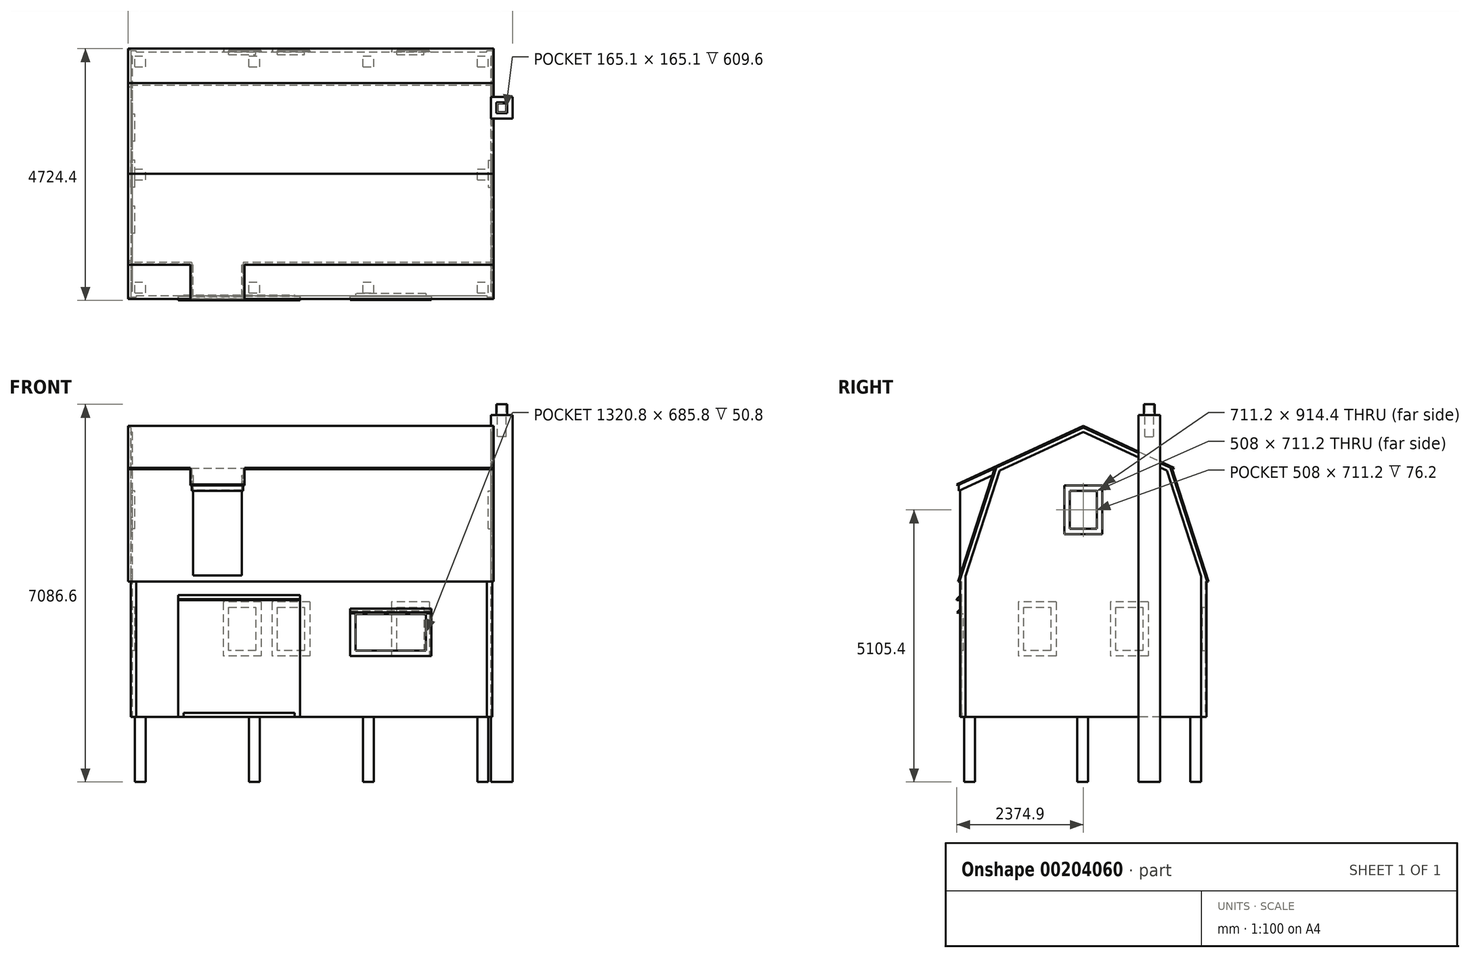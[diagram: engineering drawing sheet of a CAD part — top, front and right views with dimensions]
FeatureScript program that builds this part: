
annotation { "Feature Type Name" : "Feature", "Feature Type Description" : "" }
export const myFeature = defineFeature(function(context is Context, id is Id, definition is map)
    precondition{}
    {
        {
            var Q0;
            Q0=qCreatedBy(makeId("Right.planeOp"),FACE);
            var sketch = newSketch(context, id + "F0", { "sketchPlane" : qUnion([Q0])});
            skLineSegment(sketch, "E0", {"start": v(0, 0) * mm, "end": v(0, 2540) * mm});
            skLineSegment(sketch, "E1", {"start": v(0, 2540) * mm, "end": v(698.5, 4699) * mm});
            skLineSegment(sketch, "E2", {"start": v(698.5, 4699) * mm, "end": v(2349.5, 5461) * mm});
            skLineSegment(sketch, "E3", {"start": v(2349.5, 5461) * mm, "end": v(4000.5, 4699) * mm});
            skLineSegment(sketch, "E4", {"start": v(4000.5, 4699) * mm, "end": v(4699, 2540) * mm});
            skLineSegment(sketch, "E5", {"start": v(4699, 2540) * mm, "end": v(4699, 0) * mm});
            skLineSegment(sketch, "E6", {"start": v(4699, 0) * mm, "end": v(0, 0) * mm});
            skLineSegment(sketch, "E7", {"start": v(2349.5, 5461) * mm, "end": v(2349.5, 0) * mm, "construction": true});
            skSolve(sketch);
        }
        {
            var Q0;
            Q0 = qSketchRegion(id + "F0", true);
            extrude(context, id + "F1", {"entities" : qUnion([Q0]), "depth" : 6781.8 * mm});
        }
        {
            var Q0;
            Q0=makeQuery(id+"F1.opExtrude","CAP_FACE",FACE,{"disambiguationData":[OSD([sQuery(id+"F0.wireOp",EDGE,"E0"),sQuery(id+"F0.wireOp",EDGE,"E1"),sQuery(id+"F0.wireOp",EDGE,"E2"),sQuery(id+"F0.wireOp",EDGE,"E3"),sQuery(id+"F0.wireOp",EDGE,"E4"),sQuery(id+"F0.wireOp",EDGE,"E5"),sQuery(id+"F0.wireOp",EDGE,"E6")])],"isStart":false});
            var sketch = newSketch(context, id + "F2", { "sketchPlane" : qUnion([Q0])});
            skLineSegment(sketch, "E8.bottom", {"start": v(0, 2540) * mm, "end": v(38.1, 2540) * mm});
            skLineSegment(sketch, "E8.top", {"start": v(0, 0) * mm, "end": v(38.1, 0) * mm});
            skLineSegment(sketch, "E8.left", {"start": v(0, 2540) * mm, "end": v(0, 0) * mm});
            skLineSegment(sketch, "E8.right", {"start": v(38.1, 2540) * mm, "end": v(38.1, 0) * mm});
            skLineSegment(sketch, "E9", {"start": v(2349.5, 5461) * mm, "end": v(2349.5, 4550.7) * mm, "construction": true});
            skLineSegment(sketch, "E10.MirrorCS", {"start": v(4660.9, 2540) * mm, "end": v(4660.9, 0) * mm});
            skLineSegment(sketch, "E11.MirrorCS", {"start": v(4699, 2540) * mm, "end": v(4699, 0) * mm});
            skLineSegment(sketch, "E12.MirrorCS", {"start": v(4699, 0) * mm, "end": v(4660.9, 0) * mm});
            skLineSegment(sketch, "E13.MirrorCS", {"start": v(4699, 2540) * mm, "end": v(4660.9, 2540) * mm});
            skSolve(sketch);
        }
        {
            var Q0;
            Q0 = qSketchRegion(id + "F2", true);
            extrude(context, id + "F3", {"entities" : qUnion([Q0]), "operationType" : NewBodyOperationType.REMOVE, "endBound" : BoundingType.THROUGH_ALL, "oppositeDirection" : true, "depth" : 25.4 * mm});
        }
        {
            var Q0;
            Q0=makeQuery(id+"F1.opExtrude","CAP_FACE",FACE,{"disambiguationData":[OSD([sQuery(id+"F0.wireOp",EDGE,"E0"),sQuery(id+"F0.wireOp",EDGE,"E1"),sQuery(id+"F0.wireOp",EDGE,"E2"),sQuery(id+"F0.wireOp",EDGE,"E3"),sQuery(id+"F0.wireOp",EDGE,"E4"),sQuery(id+"F0.wireOp",EDGE,"E5"),sQuery(id+"F0.wireOp",EDGE,"E6")])],"isStart":false});
            var sketch = newSketch(context, id + "F4", { "sketchPlane" : qUnion([Q0])});
            skLineSegment(sketch, "E14", {"start": v(139.7, 0) * mm, "end": v(139.7, 2641.74) * mm});
            skLineSegment(sketch, "E15", {"start": v(139.7, 2641.74) * mm, "end": v(781.47, 4625.4) * mm});
            skLineSegment(sketch, "E16", {"start": v(781.47, 4625.4) * mm, "end": v(2349.5, 5349.1) * mm});
            skLineSegment(sketch, "E17", {"start": v(2349.5, 5349.1) * mm, "end": v(3917.53, 4625.4) * mm});
            skLineSegment(sketch, "E18", {"start": v(3917.53, 4625.4) * mm, "end": v(4559.3, 2641.74) * mm});
            skLineSegment(sketch, "E19", {"start": v(4559.3, 2641.74) * mm, "end": v(4559.3, 0) * mm});
            skSolve(sketch);
        }
        {
            var Q0;
            {var subQ0=sQuery(id+"F4.wireOp",EDGE,"E14");Q0=makeQuery(id+"F4.imprint","IMPRINT",FACE,{"disambiguationData":[TD([[makeQuery(id+"F4.imprint","IMPRINT",EDGE,{"derivedFrom":subQ0}),-1.0]])]});}
            var Q1;
            Q1 = qSketchRegion(id + "F4", true);
            extrude(context, id + "F5", {"entities" : qUnion([Q0, Q1]), "operationType" : NewBodyOperationType.REMOVE, "oppositeDirection" : true, "depth" : 25.4 * mm});
        }
        {
            var Q0;
            Q0=makeQuery(id+"F1.opExtrude","CAP_FACE",FACE,{"disambiguationData":[OSD([sQuery(id+"F0.wireOp",EDGE,"E0"),sQuery(id+"F0.wireOp",EDGE,"E1"),sQuery(id+"F0.wireOp",EDGE,"E2"),sQuery(id+"F0.wireOp",EDGE,"E3"),sQuery(id+"F0.wireOp",EDGE,"E4"),sQuery(id+"F0.wireOp",EDGE,"E5"),sQuery(id+"F0.wireOp",EDGE,"E6")])],"isStart":true});
            var sketch = newSketch(context, id + "F6", { "sketchPlane" : qUnion([Q0])});
            skLineSegment(sketch, "E20.0.0", {"start": v(-139.7, 2641.74) * mm, "end": v(-139.7, 0) * mm});
            skLineSegment(sketch, "E20.0.1", {"start": v(-139.7, 0) * mm, "end": v(-4559.3, 0) * mm});
            skLineSegment(sketch, "E20.0.2", {"start": v(-4559.3, 0) * mm, "end": v(-4559.3, 2641.74) * mm});
            skLineSegment(sketch, "E20.0.3", {"start": v(-4559.3, 2641.74) * mm, "end": v(-3917.53, 4625.4) * mm});
            skLineSegment(sketch, "E20.0.4", {"start": v(-3917.53, 4625.4) * mm, "end": v(-2349.5, 5349.1) * mm});
            skLineSegment(sketch, "E20.0.5", {"start": v(-2349.5, 5349.1) * mm, "end": v(-781.47, 4625.4) * mm});
            skLineSegment(sketch, "E20.0.6", {"start": v(-781.47, 4625.4) * mm, "end": v(-139.7, 2641.74) * mm});
            skSolve(sketch);
        }
        {
            var Q0;
            Q0 = qSketchRegion(id + "F6", true);
            extrude(context, id + "F7", {"entities" : qUnion([Q0]), "operationType" : NewBodyOperationType.REMOVE, "oppositeDirection" : true, "depth" : 25.4 * mm});
        }
        {
            var Q0;
            Q0=makeQuery(id+"F1.opExtrude","CAP_FACE",FACE,{"disambiguationData":[OSD([sQuery(id+"F0.wireOp",EDGE,"E0"),sQuery(id+"F0.wireOp",EDGE,"E1"),sQuery(id+"F0.wireOp",EDGE,"E2"),sQuery(id+"F0.wireOp",EDGE,"E3"),sQuery(id+"F0.wireOp",EDGE,"E4"),sQuery(id+"F0.wireOp",EDGE,"E5"),sQuery(id+"F0.wireOp",EDGE,"E6")])],"isStart":false});
            var sketch = newSketch(context, id + "F8", { "sketchPlane" : qUnion([Q0])});
            skLineSegment(sketch, "E21", {"start": v(26.7, 2540) * mm, "end": v(719.24, 4680.6) * mm});
            skLineSegment(sketch, "E22", {"start": v(719.24, 4680.6) * mm, "end": v(2349.5, 5433.03) * mm});
            skLineSegment(sketch, "E23", {"start": v(2349.5, 5433.03) * mm, "end": v(3979.76, 4680.6) * mm});
            skLineSegment(sketch, "E24", {"start": v(3979.76, 4680.6) * mm, "end": v(4672.3, 2540) * mm});
            skLineSegment(sketch, "E25", {"start": v(4672.3, 2540) * mm, "end": v(4699, 2540) * mm});
            skLineSegment(sketch, "E26", {"start": v(26.7, 2540) * mm, "end": v(0, 2540) * mm});
            skLineSegment(sketch, "E27", {"start": v(698.5, 4699) * mm, "end": v(645.83, 4674.7) * mm});
            skLineSegment(sketch, "E28", {"start": v(645.83, 4674.7) * mm, "end": v(656.48, 4651.63) * mm});
            skLineSegment(sketch, "E29", {"start": v(656.48, 4651.63) * mm, "end": v(687.86, 4666.11) * mm});
            skLineSegment(sketch, "E30", {"start": v(2349.5, 5433.03) * mm, "end": v(2349.5, 5286.9) * mm});
            skLineSegment(sketch, "E31.MirrorCS", {"start": v(4000.5, 4699) * mm, "end": v(4053.17, 4674.7) * mm});
            skLineSegment(sketch, "E32.MirrorCS", {"start": v(4042.52, 4651.63) * mm, "end": v(4011.14, 4666.11) * mm});
            skLineSegment(sketch, "E33.MirrorCS", {"start": v(4053.17, 4674.7) * mm, "end": v(4042.52, 4651.63) * mm});
            skSolve(sketch);
        }
        {
            var Q0;
            Q0=makeQuery(id+"F8.imprint","IMPRINT",FACE,{"disambiguationData":[TD([[makeQuery(id+"F8.imprint","IMPRINT",EDGE,{"derivedFrom":sQuery(id+"F8.wireOp",EDGE,"E21")}),1.0]])]});
            var Q1;
            {var subQ0=sQuery(id+"F8.wireOp",EDGE,"E27");Q1=makeQuery(id+"F8.imprint","IMPRINT",FACE,{"disambiguationData":[TD([[makeQuery(id+"F8.imprint","IMPRINT",EDGE,{"derivedFrom":subQ0}),1.0]])]});}
            var Q2;
            {var subQ0=sQuery(id+"F8.wireOp",EDGE,"E31.MirrorCS");Q2=makeQuery(id+"F8.imprint","IMPRINT",FACE,{"disambiguationData":[TD([[makeQuery(id+"F8.imprint","IMPRINT",EDGE,{"derivedFrom":subQ0}),-1.0]])]});}
            extrude(context, id + "F9", {"entities" : qUnion([Q0, Q1, Q2]), "operationType" : NewBodyOperationType.ADD, "depth" : 25.4 * mm, "hasSecondDirection" : true, "secondDirectionOppositeDirection" : true, "secondDirectionDepth" : 6832.6 * mm});
        }
        {
            var Q0;
            Q0=makeQuery(id+"F5.boolean.opBoolean","COPY",FACE,{"derivedFrom":makeQuery(id+"F5.opExtrude","CAP_FACE",FACE,{"disambiguationData":[OSD([sQuery(id+"F0.wireOp",EDGE,"E6"),sQuery(id+"F4.wireOp",EDGE,"E14"),sQuery(id+"F4.wireOp",EDGE,"E15"),sQuery(id+"F4.wireOp",EDGE,"E16"),sQuery(id+"F4.wireOp",EDGE,"E17"),sQuery(id+"F4.wireOp",EDGE,"E18"),sQuery(id+"F4.wireOp",EDGE,"E19")])],"isStart":false})});
            var sketch = newSketch(context, id + "F10", { "sketchPlane" : qUnion([Q0])});
            skLineSegment(sketch, "E34.bottom", {"start": v(3386.92, -1219.2) * mm, "end": v(3793.32, -1219.2) * mm});
            skLineSegment(sketch, "E34.top", {"start": v(3386.92, 5664.2) * mm, "end": v(3793.32, 5664.2) * mm});
            skLineSegment(sketch, "E34.left", {"start": v(3386.92, -1219.2) * mm, "end": v(3386.92, 5664.2) * mm});
            skLineSegment(sketch, "E34.right", {"start": v(3793.32, -1219.2) * mm, "end": v(3793.32, 5664.2) * mm});
            skSolve(sketch);
        }
        {
            var Q0;
            Q0 = qSketchRegion(id + "F10", true);
            extrude(context, id + "F11", {"entities" : qUnion([Q0]), "operationType" : NewBodyOperationType.ADD, "depth" : 406.4 * mm});
        }
        {
            var Q0;
            Q0=makeQuery(id+"F11.opExtrude","SWEPT_FACE",FACE,{"disambiguationData":[OSD([sQuery(id+"F10.wireOp",EDGE,"E34.top")])]});
            var sketch = newSketch(context, id + "F12", { "sketchPlane" : qUnion([Q0])});
            skLineSegment(sketch, "E35.0", {"start": v(6858, 3691.72) * mm, "end": v(6858, 3488.52) * mm});
            skLineSegment(sketch, "E35.1", {"start": v(7061.2, 3691.72) * mm, "end": v(6858, 3691.72) * mm});
            skLineSegment(sketch, "E35.2", {"start": v(7061.2, 3488.52) * mm, "end": v(7061.2, 3691.72) * mm});
            skLineSegment(sketch, "E35.3", {"start": v(6858, 3488.52) * mm, "end": v(7061.2, 3488.52) * mm});
            skSolve(sketch);
        }
        {
            var Q0;
            Q0 = qSketchRegion(id + "F12", true);
            extrude(context, id + "F13", {"entities" : qUnion([Q0]), "operationType" : NewBodyOperationType.ADD, "depth" : 203.2 * mm});
        }
        {
            var Q0;
            Q0=makeQuery(id+"F13.opExtrude","CAP_FACE",FACE,{"disambiguationData":[OSD([sQuery(id+"F12.wireOp",EDGE,"E35.0"),sQuery(id+"F12.wireOp",EDGE,"E35.1"),sQuery(id+"F12.wireOp",EDGE,"E35.2"),sQuery(id+"F12.wireOp",EDGE,"E35.3")])],"isStart":false});
            var sketch = newSketch(context, id + "F14", { "sketchPlane" : qUnion([Q0])});
            skLineSegment(sketch, "E36.0", {"start": v(7042.15, 3672.67) * mm, "end": v(6877.05, 3672.67) * mm});
            skLineSegment(sketch, "E36.1", {"start": v(7042.15, 3507.57) * mm, "end": v(7042.15, 3672.67) * mm});
            skLineSegment(sketch, "E36.2", {"start": v(6877.05, 3507.57) * mm, "end": v(7042.15, 3507.57) * mm});
            skLineSegment(sketch, "E36.3", {"start": v(6877.05, 3672.67) * mm, "end": v(6877.05, 3507.57) * mm});
            skSolve(sketch);
        }
        {
            var Q0;
            Q0=makeQuery(id+"F14.imprint","IMPRINT",FACE,{"disambiguationData":[TD([[makeQuery(id+"F14.imprint","IMPRINT",EDGE,{"derivedFrom":sQuery(id+"F14.wireOp",EDGE,"E36.0")}),1.0]])]});
            extrude(context, id + "F15", {"entities" : qUnion([Q0]), "operationType" : NewBodyOperationType.REMOVE, "oppositeDirection" : true, "depth" : 609.6 * mm});
        }
        {
            var Q0;
            Q0=makeQuery(id+"F7.boolean.opBoolean","COPY",FACE,{"derivedFrom":makeQuery(id+"F7.opExtrude","CAP_FACE",FACE,{"disambiguationData":[OSD([sQuery(id+"F6.wireOp",EDGE,"E20.0.0"),sQuery(id+"F6.wireOp",EDGE,"E20.0.1"),sQuery(id+"F6.wireOp",EDGE,"E20.0.2"),sQuery(id+"F6.wireOp",EDGE,"E20.0.3"),sQuery(id+"F6.wireOp",EDGE,"E20.0.4"),sQuery(id+"F6.wireOp",EDGE,"E20.0.5"),sQuery(id+"F6.wireOp",EDGE,"E20.0.6")])],"isStart":false})});
            cPlane(context, id + "F16", {"entities" : qUnion([Q0]), "cplaneType" : CPlaneType.OFFSET, "offset" : 1143 * mm, "oppositeDirection" : true, "width" : 152.4 * mm, "height" : 152.4 * mm});
        }
        {
            var Q0;
            Q0=qCreatedBy(id+"F16.planeOp",FACE);
            var sketch = newSketch(context, id + "F17", { "sketchPlane" : qUnion([Q0])});
            skLineSegment(sketch, "E37", {"start": v(-698.5, 4699) * mm, "end": v(-38.1, 4394.2) * mm});
            skLineSegment(sketch, "E38", {"start": v(-38.1, 4394.2) * mm, "end": v(-38.1, 2657.76) * mm});
            skLineSegment(sketch, "E39", {"start": v(-38.1, 2657.76) * mm, "end": v(-698.5, 4699) * mm});
            skSolve(sketch);
        }
        {
            var Q0;
            Q0 = qSketchRegion(id + "F17", true);
            extrude(context, id + "F18", {"entities" : qUnion([Q0]), "operationType" : NewBodyOperationType.ADD, "oppositeDirection" : true, "depth" : 914.4 * mm});
        }
        {
            var Q0;
            Q0=makeQuery(id+"F18.opExtrude","CAP_FACE",FACE,{"disambiguationData":[OSD([sQuery(id+"F17.wireOp",EDGE,"E37"),sQuery(id+"F17.wireOp",EDGE,"E38"),sQuery(id+"F17.wireOp",EDGE,"E39")])],"isStart":true});
            var sketch = newSketch(context, id + "F19", { "sketchPlane" : qUnion([Q0])});
            skLineSegment(sketch, "E40", {"start": v(-825.06, 4757.41) * mm, "end": v(-12.7, 4382.48) * mm});
            skLineSegment(sketch, "E41", {"start": v(-12.7, 4382.48) * mm, "end": v(-12.7, 4242.6) * mm});
            skLineSegment(sketch, "E42", {"start": v(-12.7, 4242.6) * mm, "end": v(-874.8, 4640.5) * mm});
            skLineSegment(sketch, "E43", {"start": v(-874.8, 4640.5) * mm, "end": v(-825.06, 4757.41) * mm});
            skSolve(sketch);
        }
        {
            var Q0;
            Q0 = qSketchRegion(id + "F19", true);
            extrude(context, id + "F20", {"entities" : qUnion([Q0]), "operationType" : NewBodyOperationType.ADD, "depth" : 25.4 * mm, "hasSecondDirection" : true, "secondDirectionOppositeDirection" : true, "secondDirectionDepth" : 939.8 * mm});
        }
        {
            var Q0;
            Q0=makeQuery(id+"F20.opExtrude","CAP_FACE",FACE,{"disambiguationData":[OSD([sQuery(id+"F19.wireOp",EDGE,"E40"),sQuery(id+"F19.wireOp",EDGE,"E41"),sQuery(id+"F19.wireOp",EDGE,"E42"),sQuery(id+"F19.wireOp",EDGE,"E43")])],"isStart":false});
            var sketch = newSketch(context, id + "F21", { "sketchPlane" : qUnion([Q0])});
            skLineSegment(sketch, "E44", {"start": v(-645.83, 4674.7) * mm, "end": v(23.34, 4365.84) * mm});
            skLineSegment(sketch, "E45", {"start": v(23.34, 4365.84) * mm, "end": v(12.7, 4342.78) * mm});
            skLineSegment(sketch, "E46", {"start": v(12.7, 4342.78) * mm, "end": v(-656.48, 4651.63) * mm});
            skSolve(sketch);
        }
        {
            var Q0;
            {var subQ0=sQuery(id+"F21.wireOp",EDGE,"E44");var subQ1=sQuery(id+"F19.wireOp",EDGE,"E41");var subQ2=makeQuery(id+"F20.opExtrude","CAP_EDGE",EDGE,{"disambiguationData":[OSD([subQ1])],"isStart":false});var subQ3=makeQuery(id+"F21.imprint","INTERSECT",VERTEX,{"derivedFrom":[subQ2,subQ0]});Q0=makeQuery(id+"F21.imprint","IMPRINT",FACE,{"disambiguationData":[TD([[makeQuery(id+"F21.imprint","IMPRINT",EDGE,{"disambiguationData":[TD([[subQ3,-1.0]])],"derivedFrom":subQ2}),-1.0]])]});}
            var Q1;
            {var subQ3=sQuery(id+"F21.wireOp",EDGE,"E45");Q1=makeQuery(id+"F21.imprint","IMPRINT",FACE,{"disambiguationData":[TD([[makeQuery(id+"F21.imprint","IMPRINT",EDGE,{"derivedFrom":subQ3}),-1.0]])]});}
            extrude(context, id + "F22", {"entities" : qUnion([Q0, Q1]), "operationType" : NewBodyOperationType.ADD, "depth" : 25.4 * mm, "hasSecondDirection" : true, "secondDirectionOppositeDirection" : true, "secondDirectionDepth" : 990.6 * mm});
        }
        {
            var Q0;
            Q0=makeQuery(id+"F3.boolean.opBoolean","COPY",FACE,{"derivedFrom":makeQuery(id+"F3.opExtrude","SWEPT_FACE",FACE,{"disambiguationData":[OSD([sQuery(id+"F2.wireOp",EDGE,"E8.right")])]})});
            var sketch = newSketch(context, id + "F23", { "sketchPlane" : qUnion([Q0])});
            skLineSegment(sketch, "E47", {"start": v(101.6, 0) * mm, "end": v(101.6, 2540) * mm});
            skLineSegment(sketch, "E48", {"start": v(101.6, 2540) * mm, "end": v(6680.2, 2540) * mm});
            skLineSegment(sketch, "E49", {"start": v(6680.2, 2540) * mm, "end": v(6680.2, 0) * mm});
            skSolve(sketch);
        }
        {
            var Q0;
            {var subQ0=sQuery(id+"F23.wireOp",EDGE,"E47");Q0=makeQuery(id+"F23.imprint","IMPRINT",FACE,{"disambiguationData":[TD([[makeQuery(id+"F23.imprint","IMPRINT",EDGE,{"derivedFrom":subQ0}),-1.0]])]});}
            extrude(context, id + "F24", {"entities" : qUnion([Q0]), "operationType" : NewBodyOperationType.REMOVE, "oppositeDirection" : true, "depth" : 25.4 * mm});
        }
        {
            var Q0;
            Q0=makeQuery(id+"F3.boolean.opBoolean","COPY",FACE,{"derivedFrom":makeQuery(id+"F3.opExtrude","SWEPT_FACE",FACE,{"disambiguationData":[OSD([sQuery(id+"F2.wireOp",EDGE,"E10.MirrorCS")])]})});
            var sketch = newSketch(context, id + "F25", { "sketchPlane" : qUnion([Q0])});
            skLineSegment(sketch, "E50.0.0", {"start": v(-101.6, 2540) * mm, "end": v(-101.6, 0) * mm});
            skLineSegment(sketch, "E50.0.1", {"start": v(-101.6, 0) * mm, "end": v(-6680.2, 0) * mm});
            skLineSegment(sketch, "E50.0.2", {"start": v(-6680.2, 0) * mm, "end": v(-6680.2, 2540) * mm});
            skLineSegment(sketch, "E50.0.3", {"start": v(-6680.2, 2540) * mm, "end": v(-101.6, 2540) * mm});
            skSolve(sketch);
        }
        {
            var Q0;
            Q0 = qSketchRegion(id + "F25", true);
            extrude(context, id + "F26", {"entities" : qUnion([Q0]), "operationType" : NewBodyOperationType.REMOVE, "oppositeDirection" : true, "depth" : 25.4 * mm});
        }
        {
            var Q0;
            Q0=makeQuery(id+"F24.boolean.opBoolean","COPY",FACE,{"derivedFrom":makeQuery(id+"F24.opExtrude","CAP_FACE",FACE,{"disambiguationData":[OSD([sQuery(id+"F0.wireOp",EDGE,"E6"),sQuery(id+"F2.wireOp",EDGE,"E8.top"),sQuery(id+"F2.wireOp",EDGE,"E8.right"),sQuery(id+"F23.wireOp",EDGE,"E47"),sQuery(id+"F23.wireOp",EDGE,"E48"),sQuery(id+"F23.wireOp",EDGE,"E49")])],"isStart":false})});
            var sketch = newSketch(context, id + "F27", { "sketchPlane" : qUnion([Q0])});
            skLineSegment(sketch, "E51.bottom", {"start": v(889, 0) * mm, "end": v(3175, 0) * mm});
            skLineSegment(sketch, "E51.top", {"start": v(889, 2286) * mm, "end": v(3175, 2286) * mm});
            skLineSegment(sketch, "E51.left", {"start": v(889, 0) * mm, "end": v(889, 2286) * mm});
            skLineSegment(sketch, "E51.right", {"start": v(3175, 0) * mm, "end": v(3175, 2286) * mm});
            skLineSegment(sketch, "E52.bottom", {"start": v(4114.8, 2032) * mm, "end": v(5638.8, 2032) * mm});
            skLineSegment(sketch, "E52.top", {"start": v(4114.8, 1143) * mm, "end": v(5638.8, 1143) * mm});
            skLineSegment(sketch, "E52.left", {"start": v(4114.8, 2032) * mm, "end": v(4114.8, 1143) * mm});
            skLineSegment(sketch, "E52.right", {"start": v(5638.8, 2032) * mm, "end": v(5638.8, 1143) * mm});
            skSolve(sketch);
        }
        {
            var Q0;
            Q0 = qSketchRegion(id + "F27", true);
            extrude(context, id + "F28", {"entities" : qUnion([Q0]), "operationType" : NewBodyOperationType.ADD, "depth" : 12.7 * mm});
        }
        {
            var Q0;
            Q0=makeQuery(id+"F28.opExtrude","CAP_FACE",FACE,{"disambiguationData":[OSD([sQuery(id+"F27.wireOp",EDGE,"E52.bottom"),sQuery(id+"F27.wireOp",EDGE,"E52.top"),sQuery(id+"F27.wireOp",EDGE,"E52.left"),sQuery(id+"F27.wireOp",EDGE,"E52.right")])],"isStart":false});
            var sketch = newSketch(context, id + "F29", { "sketchPlane" : qUnion([Q0])});
            skLineSegment(sketch, "E53.0", {"start": v(5537.2, 1930.4) * mm, "end": v(4216.4, 1930.4) * mm});
            skLineSegment(sketch, "E53.1", {"start": v(5537.2, 1244.6) * mm, "end": v(5537.2, 1930.4) * mm});
            skLineSegment(sketch, "E53.2", {"start": v(4216.4, 1244.6) * mm, "end": v(5537.2, 1244.6) * mm});
            skLineSegment(sketch, "E53.3", {"start": v(4216.4, 1930.4) * mm, "end": v(4216.4, 1244.6) * mm});
            skSolve(sketch);
        }
        {
            var Q0;
            Q0 = qSketchRegion(id + "F29", true);
            extrude(context, id + "F30", {"entities" : qUnion([Q0]), "operationType" : NewBodyOperationType.REMOVE, "oppositeDirection" : true, "depth" : 50.8 * mm});
        }
        {
            var Q0;
            Q0=makeQuery(id+"F28.opExtrude","SWEPT_FACE",FACE,{"disambiguationData":[OSD([sQuery(id+"F27.wireOp",EDGE,"E52.right")])]});
            var sketch = newSketch(context, id + "F31", { "sketchPlane" : qUnion([Q0])});
            skLineSegment(sketch, "E54", {"start": v(50.8, 2032) * mm, "end": v(-17.96, 1963.24) * mm});
            skLineSegment(sketch, "E55", {"start": v(-17.96, 1963.24) * mm, "end": v(0, 1945.28) * mm});
            skLineSegment(sketch, "E56", {"start": v(0, 1945.28) * mm, "end": v(50.8, 1996.08) * mm});
            skLineSegment(sketch, "E57", {"start": v(50.8, 1996.08) * mm, "end": v(50.8, 2032) * mm});
            skSolve(sketch);
        }
        {
            var Q0;
            Q0 = qSketchRegion(id + "F31", true);
            var Q1;
            Q1=makeQuery(id+"F28.opExtrude","CAP_VERTEX",VERTEX,{"disambiguationData":[OSD([sQuery(id+"F27.wireOp",EDGE,"E52.bottom"),sQuery(id+"F27.wireOp",EDGE,"E52.left")])],"isStart":false});
            extrude(context, id + "F32", {"entities" : qUnion([Q0]), "operationType" : NewBodyOperationType.ADD, "endBound" : BoundingType.UP_TO_VERTEX, "oppositeDirection" : true, "endBoundEntityVertex" : qUnion([Q1]), "depth" : 25.4 * mm});
        }
        {
            var Q0;
            Q0=makeQuery(id+"F28.opExtrude","SWEPT_FACE",FACE,{"disambiguationData":[OSD([sQuery(id+"F27.wireOp",EDGE,"E51.left")])]});
            var sketch = newSketch(context, id + "F33", { "sketchPlane" : qUnion([Q0])});
            skLineSegment(sketch, "E58", {"start": v(-50.8, 2286) * mm, "end": v(25.4, 2209.8) * mm});
            skLineSegment(sketch, "E59", {"start": v(25.4, 2209.8) * mm, "end": v(25.4, 2190.75) * mm});
            skLineSegment(sketch, "E60", {"start": v(25.4, 2190.75) * mm, "end": v(-50.8, 2190.75) * mm});
            skSolve(sketch);
        }
        {
            var Q0;
            {var subQ0=sQuery(id+"F33.wireOp",EDGE,"E58");Q0=makeQuery(id+"F33.imprint","IMPRINT",FACE,{"disambiguationData":[TD([[makeQuery(id+"F33.imprint","IMPRINT",EDGE,{"derivedFrom":subQ0}),-1.0]])]});}
            var Q1;
            Q1=makeQuery(id+"F28.opExtrude","CAP_VERTEX",VERTEX,{"disambiguationData":[OSD([sQuery(id+"F27.wireOp",EDGE,"E51.top"),sQuery(id+"F27.wireOp",EDGE,"E51.right")])],"isStart":true});
            extrude(context, id + "F34", {"entities" : qUnion([Q0]), "operationType" : NewBodyOperationType.ADD, "endBound" : BoundingType.UP_TO_VERTEX, "oppositeDirection" : true, "endBoundEntityVertex" : qUnion([Q1]), "depth" : 25.4 * mm});
        }
        {
            var Q0;
            {var subQ0=sQuery(id+"F4.wireOp",EDGE,"E16");var subQ1=sQuery(id+"F4.wireOp",EDGE,"E15");var subQ2=sQuery(id+"F4.wireOp",EDGE,"E14");var subQ3=sQuery(id+"F0.wireOp",EDGE,"E6");var subQ4=sQuery(id+"F4.wireOp",EDGE,"E17");Q0=makeQuery(id+"F11.boolean.opBoolean","SPLIT",FACE,{"disambiguationData":[TD([makeQuery(id+"F5.boolean.opBoolean","COPY",FACE,{"derivedFrom":makeQuery(id+"F5.opExtrude","SWEPT_FACE",FACE,{"disambiguationData":[OSD([subQ2])]})})])],"derivedFrom":makeQuery(id+"F5.boolean.opBoolean","COPY",FACE,{"derivedFrom":makeQuery(id+"F5.opExtrude","CAP_FACE",FACE,{"disambiguationData":[OSD([subQ3,subQ2,subQ1,subQ0,subQ4,sQuery(id+"F4.wireOp",EDGE,"E18"),sQuery(id+"F4.wireOp",EDGE,"E19")])],"isStart":false})})});}
            var sketch = newSketch(context, id + "F35", { "sketchPlane" : qUnion([Q0])});
            skLineSegment(sketch, "E61.bottom", {"start": v(1993.9, 4343.4) * mm, "end": v(2705.1, 4343.4) * mm});
            skLineSegment(sketch, "E61.top", {"start": v(1993.9, 3429) * mm, "end": v(2705.1, 3429) * mm});
            skLineSegment(sketch, "E61.left", {"start": v(1993.9, 4343.4) * mm, "end": v(1993.9, 3429) * mm});
            skLineSegment(sketch, "E61.right", {"start": v(2705.1, 4343.4) * mm, "end": v(2705.1, 3429) * mm});
            skLineSegment(sketch, "E62", {"start": v(2349.5, 5349.1) * mm, "end": v(2349.5, 4343.4) * mm, "construction": true});
            skSolve(sketch);
        }
        {
            var Q0;
            Q0 = qSketchRegion(id + "F35", true);
            extrude(context, id + "F36", {"entities" : qUnion([Q0]), "operationType" : NewBodyOperationType.ADD, "depth" : 25.4 * mm});
        }
        {
            var Q0;
            Q0=makeQuery(id+"F36.opExtrude","CAP_FACE",FACE,{"disambiguationData":[OSD([sQuery(id+"F35.wireOp",EDGE,"E61.bottom"),sQuery(id+"F35.wireOp",EDGE,"E61.top"),sQuery(id+"F35.wireOp",EDGE,"E61.left"),sQuery(id+"F35.wireOp",EDGE,"E61.right")])],"isStart":false});
            var sketch = newSketch(context, id + "F37", { "sketchPlane" : qUnion([Q0])});
            skLineSegment(sketch, "E63.0", {"start": v(2603.5, 4241.8) * mm, "end": v(2095.5, 4241.8) * mm});
            skLineSegment(sketch, "E63.1", {"start": v(2603.5, 3530.6) * mm, "end": v(2603.5, 4241.8) * mm});
            skLineSegment(sketch, "E63.2", {"start": v(2095.5, 3530.6) * mm, "end": v(2603.5, 3530.6) * mm});
            skLineSegment(sketch, "E63.3", {"start": v(2095.5, 4241.8) * mm, "end": v(2095.5, 3530.6) * mm});
            skSolve(sketch);
        }
        {
            var Q0;
            Q0 = qSketchRegion(id + "F37", true);
            extrude(context, id + "F38", {"entities" : qUnion([Q0]), "operationType" : NewBodyOperationType.REMOVE, "oppositeDirection" : true, "depth" : 76.2 * mm});
        }
        {
            var Q0;
            Q0=makeQuery(id+"F26.boolean.opBoolean","COPY",FACE,{"derivedFrom":makeQuery(id+"F26.opExtrude","CAP_FACE",FACE,{"disambiguationData":[OSD([sQuery(id+"F25.wireOp",EDGE,"E50.0.0"),sQuery(id+"F25.wireOp",EDGE,"E50.0.1"),sQuery(id+"F25.wireOp",EDGE,"E50.0.2"),sQuery(id+"F25.wireOp",EDGE,"E50.0.3")])],"isStart":false})});
            var sketch = newSketch(context, id + "F39", { "sketchPlane" : qUnion([Q0])});
            skLineSegment(sketch, "E64.bottom", {"start": v(-5602.51, 2159) * mm, "end": v(-4891.31, 2159) * mm});
            skLineSegment(sketch, "E64.top", {"start": v(-5602.51, 1143) * mm, "end": v(-4891.31, 1143) * mm});
            skLineSegment(sketch, "E64.left", {"start": v(-5602.51, 2159) * mm, "end": v(-5602.51, 1143) * mm});
            skLineSegment(sketch, "E64.right", {"start": v(-4891.31, 2159) * mm, "end": v(-4891.31, 1143) * mm});
            skLineSegment(sketch, "E65.bottom", {"start": v(-3361.9, 2159) * mm, "end": v(-2650.7, 2159) * mm});
            skLineSegment(sketch, "E65.top", {"start": v(-3361.9, 1143) * mm, "end": v(-2650.7, 1143) * mm});
            skLineSegment(sketch, "E65.left", {"start": v(-3361.9, 2159) * mm, "end": v(-3361.9, 1143) * mm});
            skLineSegment(sketch, "E65.right", {"start": v(-2650.7, 2159) * mm, "end": v(-2650.7, 1143) * mm});
            skLineSegment(sketch, "E66.bottom", {"start": v(-2447.5, 2159) * mm, "end": v(-1736.3, 2159) * mm});
            skLineSegment(sketch, "E66.top", {"start": v(-2447.5, 1143) * mm, "end": v(-1736.3, 1143) * mm});
            skLineSegment(sketch, "E66.left", {"start": v(-2447.5, 2159) * mm, "end": v(-2447.5, 1143) * mm});
            skLineSegment(sketch, "E66.right", {"start": v(-1736.3, 2159) * mm, "end": v(-1736.3, 1143) * mm});
            skSolve(sketch);
        }
        {
            var Q0;
            Q0 = qSketchRegion(id + "F39", true);
            extrude(context, id + "F40", {"entities" : qUnion([Q0]), "operationType" : NewBodyOperationType.ADD, "depth" : 25.4 * mm});
        }
        {
            var Q0;
            Q0=makeQuery(id+"F40.opExtrude","CAP_FACE",FACE,{"disambiguationData":[OSD([sQuery(id+"F39.wireOp",EDGE,"E64.bottom"),sQuery(id+"F39.wireOp",EDGE,"E64.top"),sQuery(id+"F39.wireOp",EDGE,"E64.left"),sQuery(id+"F39.wireOp",EDGE,"E64.right")])],"isStart":false});
            var sketch = newSketch(context, id + "F41", { "sketchPlane" : qUnion([Q0])});
            skLineSegment(sketch, "E67.0", {"start": v(-4992.91, 2057.4) * mm, "end": v(-5500.91, 2057.4) * mm});
            skLineSegment(sketch, "E67.1", {"start": v(-4992.91, 1244.6) * mm, "end": v(-4992.91, 2057.4) * mm});
            skLineSegment(sketch, "E67.2", {"start": v(-5500.91, 1244.6) * mm, "end": v(-4992.91, 1244.6) * mm});
            skLineSegment(sketch, "E67.3", {"start": v(-5500.91, 2057.4) * mm, "end": v(-5500.91, 1244.6) * mm});
            skLineSegment(sketch, "E68.0", {"start": v(-2752.3, 2057.4) * mm, "end": v(-3260.3, 2057.4) * mm});
            skLineSegment(sketch, "E68.1", {"start": v(-2752.3, 1244.6) * mm, "end": v(-2752.3, 2057.4) * mm});
            skLineSegment(sketch, "E68.2", {"start": v(-3260.3, 1244.6) * mm, "end": v(-2752.3, 1244.6) * mm});
            skLineSegment(sketch, "E68.3", {"start": v(-3260.3, 2057.4) * mm, "end": v(-3260.3, 1244.6) * mm});
            skLineSegment(sketch, "E69.0", {"start": v(-1837.9, 2057.4) * mm, "end": v(-2345.9, 2057.4) * mm});
            skLineSegment(sketch, "E69.1", {"start": v(-1837.9, 1244.6) * mm, "end": v(-1837.9, 2057.4) * mm});
            skLineSegment(sketch, "E69.2", {"start": v(-2345.9, 1244.6) * mm, "end": v(-1837.9, 1244.6) * mm});
            skLineSegment(sketch, "E69.3", {"start": v(-2345.9, 2057.4) * mm, "end": v(-2345.9, 1244.6) * mm});
            skSolve(sketch);
        }
        {
            var Q0;
            Q0 = qSketchRegion(id + "F41", true);
            extrude(context, id + "F42", {"entities" : qUnion([Q0]), "operationType" : NewBodyOperationType.REMOVE, "oppositeDirection" : true, "depth" : 76.2 * mm});
        }
        {
            var Q0;
            Q0=makeQuery(id+"F7.boolean.opBoolean","COPY",FACE,{"derivedFrom":makeQuery(id+"F7.opExtrude","CAP_FACE",FACE,{"disambiguationData":[OSD([sQuery(id+"F6.wireOp",EDGE,"E20.0.0"),sQuery(id+"F6.wireOp",EDGE,"E20.0.1"),sQuery(id+"F6.wireOp",EDGE,"E20.0.2"),sQuery(id+"F6.wireOp",EDGE,"E20.0.3"),sQuery(id+"F6.wireOp",EDGE,"E20.0.4"),sQuery(id+"F6.wireOp",EDGE,"E20.0.5"),sQuery(id+"F6.wireOp",EDGE,"E20.0.6")])],"isStart":false})});
            var sketch = newSketch(context, id + "F43", { "sketchPlane" : qUnion([Q0])});
            skLineSegment(sketch, "E70.0.0", {"start": v(-2705.1, 4343.4) * mm, "end": v(-1993.9, 4343.4) * mm});
            skLineSegment(sketch, "E70.0.1", {"start": v(-1993.9, 4343.4) * mm, "end": v(-1993.9, 3429) * mm});
            skLineSegment(sketch, "E70.0.2", {"start": v(-1993.9, 3429) * mm, "end": v(-2705.1, 3429) * mm});
            skLineSegment(sketch, "E70.0.3", {"start": v(-2705.1, 3429) * mm, "end": v(-2705.1, 4343.4) * mm});
            skLineSegment(sketch, "E71.0.0", {"start": v(-2603.5, 3530.6) * mm, "end": v(-2603.5, 4241.8) * mm});
            skLineSegment(sketch, "E71.0.1", {"start": v(-2603.5, 4241.8) * mm, "end": v(-2095.5, 4241.8) * mm});
            skLineSegment(sketch, "E71.0.2", {"start": v(-2095.5, 4241.8) * mm, "end": v(-2095.5, 3530.6) * mm});
            skLineSegment(sketch, "E71.0.3", {"start": v(-2095.5, 3530.6) * mm, "end": v(-2603.5, 3530.6) * mm});
            skSolve(sketch);
        }
        {
            var Q0;
            Q0=makeQuery(id+"F43.imprint","IMPRINT",FACE,{"disambiguationData":[TD([[makeQuery(id+"F43.imprint","IMPRINT",EDGE,{"derivedFrom":sQuery(id+"F43.wireOp",EDGE,"E71.0.0")}),-1.0]])]});
            extrude(context, id + "F44", {"entities" : qUnion([Q0]), "operationType" : NewBodyOperationType.REMOVE, "oppositeDirection" : true, "depth" : 50.8 * mm});
        }
        {
            var Q0;
            Q0 = qSketchRegion(id + "F43", true);
            extrude(context, id + "F45", {"entities" : qUnion([Q0]), "operationType" : NewBodyOperationType.ADD, "depth" : 25.4 * mm});
        }
        {
            var Q0;
            Q0=makeQuery(id+"F7.boolean.opBoolean","COPY",FACE,{"derivedFrom":makeQuery(id+"F7.opExtrude","CAP_FACE",FACE,{"disambiguationData":[OSD([sQuery(id+"F6.wireOp",EDGE,"E20.0.0"),sQuery(id+"F6.wireOp",EDGE,"E20.0.1"),sQuery(id+"F6.wireOp",EDGE,"E20.0.2"),sQuery(id+"F6.wireOp",EDGE,"E20.0.3"),sQuery(id+"F6.wireOp",EDGE,"E20.0.4"),sQuery(id+"F6.wireOp",EDGE,"E20.0.5"),sQuery(id+"F6.wireOp",EDGE,"E20.0.6")])],"isStart":false})});
            var sketch = newSketch(context, id + "F46", { "sketchPlane" : qUnion([Q0])});
            skLineSegment(sketch, "E72.bottom", {"start": v(-3568.7, 2159) * mm, "end": v(-2857.5, 2159) * mm});
            skLineSegment(sketch, "E72.top", {"start": v(-3568.7, 1143) * mm, "end": v(-2857.5, 1143) * mm});
            skLineSegment(sketch, "E72.left", {"start": v(-3568.7, 2159) * mm, "end": v(-3568.7, 1143) * mm});
            skLineSegment(sketch, "E72.right", {"start": v(-2857.5, 2159) * mm, "end": v(-2857.5, 1143) * mm});
            skLineSegment(sketch, "E73.bottom", {"start": v(-1841.5, 2159) * mm, "end": v(-1130.3, 2159) * mm});
            skLineSegment(sketch, "E73.top", {"start": v(-1841.5, 1143) * mm, "end": v(-1130.3, 1143) * mm});
            skLineSegment(sketch, "E73.left", {"start": v(-1841.5, 2159) * mm, "end": v(-1841.5, 1143) * mm});
            skLineSegment(sketch, "E73.right", {"start": v(-1130.3, 2159) * mm, "end": v(-1130.3, 1143) * mm});
            skLineSegment(sketch, "E74", {"start": v(-1841.5, 2159) * mm, "end": v(-2857.5, 2159) * mm, "construction": true});
            skLineSegment(sketch, "E75", {"start": v(-2349.5, 3429) * mm, "end": v(-2349.5, 2159) * mm, "construction": true});
            skSolve(sketch);
        }
        {
            var Q0;
            Q0 = qSketchRegion(id + "F46", true);
            extrude(context, id + "F47", {"entities" : qUnion([Q0]), "operationType" : NewBodyOperationType.ADD, "depth" : 25.4 * mm});
        }
        {
            var Q0;
            Q0=makeQuery(id+"F47.opExtrude","CAP_FACE",FACE,{"disambiguationData":[OSD([sQuery(id+"F46.wireOp",EDGE,"E72.bottom"),sQuery(id+"F46.wireOp",EDGE,"E72.top"),sQuery(id+"F46.wireOp",EDGE,"E72.left"),sQuery(id+"F46.wireOp",EDGE,"E72.right")])],"isStart":false});
            var sketch = newSketch(context, id + "F48", { "sketchPlane" : qUnion([Q0])});
            skLineSegment(sketch, "E76.0", {"start": v(-2959.1, 2057.4) * mm, "end": v(-3467.1, 2057.4) * mm});
            skLineSegment(sketch, "E76.1", {"start": v(-2959.1, 1244.6) * mm, "end": v(-2959.1, 2057.4) * mm});
            skLineSegment(sketch, "E76.2", {"start": v(-3467.1, 1244.6) * mm, "end": v(-2959.1, 1244.6) * mm});
            skLineSegment(sketch, "E76.3", {"start": v(-3467.1, 2057.4) * mm, "end": v(-3467.1, 1244.6) * mm});
            skLineSegment(sketch, "E77.0", {"start": v(-1231.9, 2057.4) * mm, "end": v(-1739.9, 2057.4) * mm});
            skLineSegment(sketch, "E77.1", {"start": v(-1231.9, 1244.6) * mm, "end": v(-1231.9, 2057.4) * mm});
            skLineSegment(sketch, "E77.2", {"start": v(-1739.9, 1244.6) * mm, "end": v(-1231.9, 1244.6) * mm});
            skLineSegment(sketch, "E77.3", {"start": v(-1739.9, 2057.4) * mm, "end": v(-1739.9, 1244.6) * mm});
            skSolve(sketch);
        }
        {
            var Q0;
            Q0 = qSketchRegion(id + "F48", true);
            extrude(context, id + "F49", {"entities" : qUnion([Q0]), "operationType" : NewBodyOperationType.REMOVE, "oppositeDirection" : true, "depth" : 76.2 * mm});
        }
        {
            var Q0;
            Q0=makeQuery(id+"F28.boolean.opBoolean","MERGE",FACE,{"derivedFrom":[makeQuery(id+"F1.opExtrude","SWEPT_FACE",FACE,{"disambiguationData":[OSD([sQuery(id+"F0.wireOp",EDGE,"E6")])]}),makeQuery(id+"F28.opExtrude","SWEPT_FACE",FACE,{"disambiguationData":[OSD([sQuery(id+"F27.wireOp",EDGE,"E51.bottom")])]})]});
            var sketch = newSketch(context, id + "F50", { "sketchPlane" : qUnion([Q0])});
            skLineSegment(sketch, "E78.bottom", {"start": v(76.2, -114.3) * mm, "end": v(279.4, -114.3) * mm});
            skLineSegment(sketch, "E78.top", {"start": v(76.2, -317.5) * mm, "end": v(279.4, -317.5) * mm});
            skLineSegment(sketch, "E78.left", {"start": v(76.2, -114.3) * mm, "end": v(76.2, -317.5) * mm});
            skLineSegment(sketch, "E78.right", {"start": v(279.4, -114.3) * mm, "end": v(279.4, -317.5) * mm});
            skLineSegment(sketch, "E79.bottom", {"start": v(2218.27, -114.3) * mm, "end": v(2421.47, -114.3) * mm});
            skLineSegment(sketch, "E79.top", {"start": v(2218.27, -317.5) * mm, "end": v(2421.47, -317.5) * mm});
            skLineSegment(sketch, "E79.left", {"start": v(2218.27, -114.3) * mm, "end": v(2218.27, -317.5) * mm});
            skLineSegment(sketch, "E79.right", {"start": v(2421.47, -114.3) * mm, "end": v(2421.47, -317.5) * mm});
            skLineSegment(sketch, "E80.bottom", {"start": v(4360.33, -114.3) * mm, "end": v(4563.53, -114.3) * mm});
            skLineSegment(sketch, "E80.top", {"start": v(4360.33, -317.5) * mm, "end": v(4563.53, -317.5) * mm});
            skLineSegment(sketch, "E80.left", {"start": v(4360.33, -114.3) * mm, "end": v(4360.33, -317.5) * mm});
            skLineSegment(sketch, "E80.right", {"start": v(4563.53, -114.3) * mm, "end": v(4563.53, -317.5) * mm});
            skLineSegment(sketch, "E81.bottom", {"start": v(6502.4, -114.3) * mm, "end": v(6705.6, -114.3) * mm});
            skLineSegment(sketch, "E81.top", {"start": v(6502.4, -317.5) * mm, "end": v(6705.6, -317.5) * mm});
            skLineSegment(sketch, "E81.left", {"start": v(6502.4, -114.3) * mm, "end": v(6502.4, -317.5) * mm});
            skLineSegment(sketch, "E81.right", {"start": v(6705.6, -114.3) * mm, "end": v(6705.6, -317.5) * mm});
            skLineSegment(sketch, "E82.bottom", {"start": v(6502.4, -2235.2) * mm, "end": v(6705.6, -2235.2) * mm});
            skLineSegment(sketch, "E82.top", {"start": v(6502.4, -2438.4) * mm, "end": v(6705.6, -2438.4) * mm});
            skLineSegment(sketch, "E82.left", {"start": v(6502.4, -2235.2) * mm, "end": v(6502.4, -2438.4) * mm});
            skLineSegment(sketch, "E82.right", {"start": v(6705.6, -2235.2) * mm, "end": v(6705.6, -2438.4) * mm});
            skLineSegment(sketch, "E83.bottom", {"start": v(76.2, -2235.2) * mm, "end": v(279.4, -2235.2) * mm});
            skLineSegment(sketch, "E83.top", {"start": v(76.2, -2438.4) * mm, "end": v(279.4, -2438.4) * mm});
            skLineSegment(sketch, "E83.left", {"start": v(76.2, -2235.2) * mm, "end": v(76.2, -2438.4) * mm});
            skLineSegment(sketch, "E83.right", {"start": v(279.4, -2235.2) * mm, "end": v(279.4, -2438.4) * mm});
            skLineSegment(sketch, "E84.bottom", {"start": v(76.2, -4356.1) * mm, "end": v(279.4, -4356.1) * mm});
            skLineSegment(sketch, "E84.top", {"start": v(76.2, -4559.3) * mm, "end": v(279.4, -4559.3) * mm});
            skLineSegment(sketch, "E84.left", {"start": v(76.2, -4356.1) * mm, "end": v(76.2, -4559.3) * mm});
            skLineSegment(sketch, "E84.right", {"start": v(279.4, -4356.1) * mm, "end": v(279.4, -4559.3) * mm});
            skLineSegment(sketch, "E85.bottom", {"start": v(2218.27, -4356.1) * mm, "end": v(2421.47, -4356.1) * mm});
            skLineSegment(sketch, "E85.top", {"start": v(2218.27, -4559.3) * mm, "end": v(2421.47, -4559.3) * mm});
            skLineSegment(sketch, "E85.left", {"start": v(2218.27, -4356.1) * mm, "end": v(2218.27, -4559.3) * mm});
            skLineSegment(sketch, "E85.right", {"start": v(2421.47, -4356.1) * mm, "end": v(2421.47, -4559.3) * mm});
            skLineSegment(sketch, "E86.bottom", {"start": v(4360.33, -4356.1) * mm, "end": v(4563.53, -4356.1) * mm});
            skLineSegment(sketch, "E86.top", {"start": v(4360.33, -4559.3) * mm, "end": v(4563.53, -4559.3) * mm});
            skLineSegment(sketch, "E86.left", {"start": v(4360.33, -4356.1) * mm, "end": v(4360.33, -4559.3) * mm});
            skLineSegment(sketch, "E86.right", {"start": v(4563.53, -4356.1) * mm, "end": v(4563.53, -4559.3) * mm});
            skLineSegment(sketch, "E87.bottom", {"start": v(6502.4, -4356.1) * mm, "end": v(6705.6, -4356.1) * mm});
            skLineSegment(sketch, "E87.top", {"start": v(6502.4, -4559.3) * mm, "end": v(6705.6, -4559.3) * mm});
            skLineSegment(sketch, "E87.left", {"start": v(6502.4, -4356.1) * mm, "end": v(6502.4, -4559.3) * mm});
            skLineSegment(sketch, "E87.right", {"start": v(6705.6, -4356.1) * mm, "end": v(6705.6, -4559.3) * mm});
            skLineSegment(sketch, "E88", {"start": v(6502.4, -317.5) * mm, "end": v(4563.53, -317.5) * mm, "construction": true});
            skLineSegment(sketch, "E89", {"start": v(4360.33, -317.5) * mm, "end": v(2421.47, -317.5) * mm, "construction": true});
            skLineSegment(sketch, "E90", {"start": v(2218.27, -317.5) * mm, "end": v(279.4, -317.5) * mm, "construction": true});
            skLineSegment(sketch, "E91", {"start": v(279.4, -317.5) * mm, "end": v(279.4, -2235.2) * mm, "construction": true});
            skLineSegment(sketch, "E92", {"start": v(279.4, -2438.4) * mm, "end": v(279.4, -4356.1) * mm, "construction": true});
            skSolve(sketch);
        }
        {
            var Q0;
            Q0 = qSketchRegion(id + "F50", true);
            extrude(context, id + "F51", {"entities" : qUnion([Q0]), "operationType" : NewBodyOperationType.ADD, "depth" : 1219.2 * mm});
        }
        {
            var Q0;
            Q0=makeQuery(id+"F28.opExtrude","CAP_FACE",FACE,{"disambiguationData":[OSD([sQuery(id+"F27.wireOp",EDGE,"E51.bottom"),sQuery(id+"F27.wireOp",EDGE,"E51.top"),sQuery(id+"F27.wireOp",EDGE,"E51.left"),sQuery(id+"F27.wireOp",EDGE,"E51.right")])],"isStart":false});
            var sketch = newSketch(context, id + "F52", { "sketchPlane" : qUnion([Q0])});
            skLineSegment(sketch, "E93.bottom", {"start": v(990.6, 0) * mm, "end": v(3073.4, 0) * mm});
            skLineSegment(sketch, "E93.top", {"start": v(990.6, 76.2) * mm, "end": v(3073.4, 76.2) * mm});
            skLineSegment(sketch, "E93.left", {"start": v(990.6, 0) * mm, "end": v(990.6, 76.2) * mm});
            skLineSegment(sketch, "E93.right", {"start": v(3073.4, 0) * mm, "end": v(3073.4, 76.2) * mm});
            skSolve(sketch);
        }
        {
            var Q0;
            Q0=makeQuery(id+"F52.imprint","IMPRINT",FACE,{"disambiguationData":[TD([[makeQuery(id+"F52.imprint","IMPRINT",EDGE,{"derivedFrom":sQuery(id+"F52.wireOp",EDGE,"E93.bottom")}),1.0]])]});
            extrude(context, id + "F53", {"entities" : qUnion([Q0]), "operationType" : NewBodyOperationType.REMOVE, "oppositeDirection" : true, "depth" : 25.4 * mm});
        }
    });
